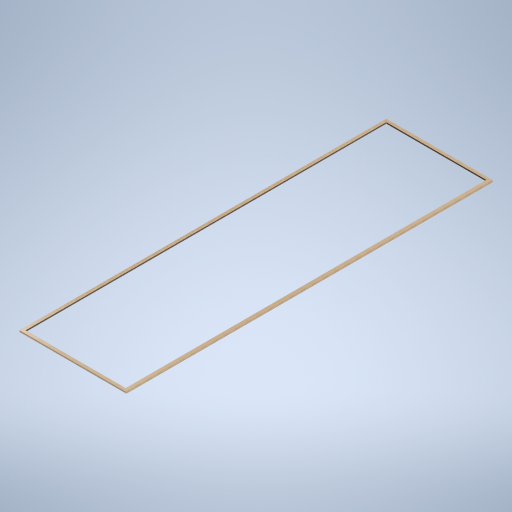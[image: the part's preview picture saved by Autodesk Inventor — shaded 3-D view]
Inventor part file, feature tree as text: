
AUTODESK INVENTOR PART (.ipt)
format: ipt  version: 2024.2 (Build 282272000, 272)  size: 280,064 bytes
history: native  units: mm
features: extrude x2, sketch x2, projected_geometry x1
ambient origin geometry x8: Origin, YZ Plane, XZ Plane, XY Plane, X Axis, Y Axis, Z Axis, Center Point
bodies: Solid1 (feature_tree)
feature tree (5):
  extrude  "Extrusion1"  Depth=8834.0mm
  extrude  "Extrusion4"  TaperAngle=0.0deg  [1 undecoded]
  sketch  "Sketch1"  dims[d1=32302.0mm d2=0.0mm d11=8834.0mm]
  sketch  "Sketch2"  dims[d12=31802.0mm d13=0.0mm d14=0.0mm]
  projected_geometry  "Projected Loop1"
note: 1 required parameter value undecoded (feature->parameter linkage not recoverable at this tier; creation-order binding heuristic only, values carry confidence <= 0.55)
